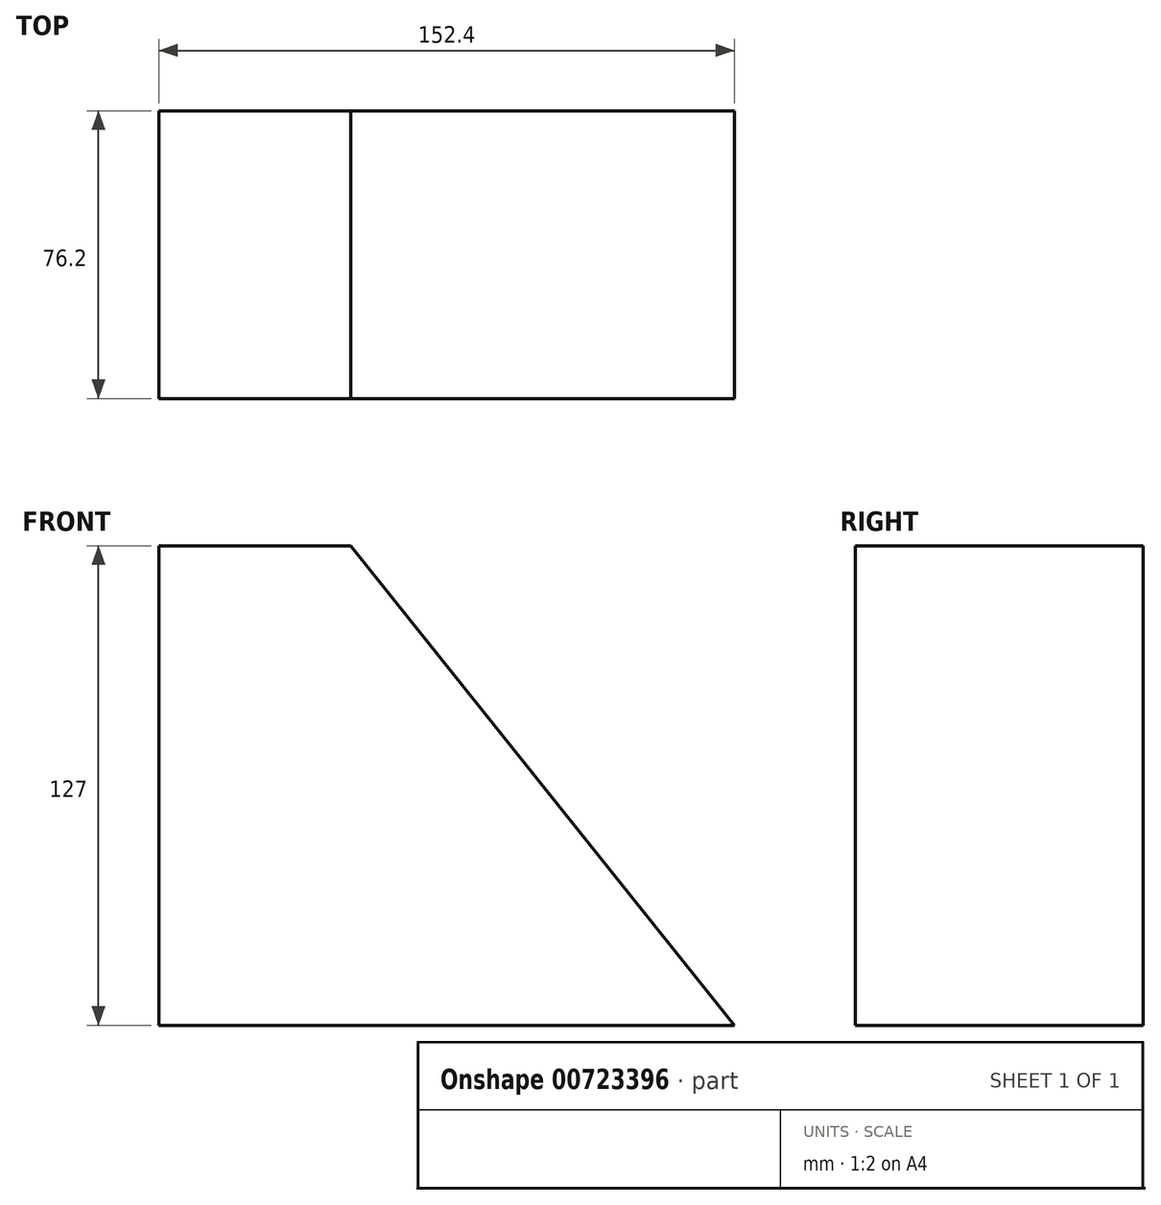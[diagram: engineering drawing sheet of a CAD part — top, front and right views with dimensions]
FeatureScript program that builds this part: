
annotation { "Feature Type Name" : "Feature", "Feature Type Description" : "" }
export const myFeature = defineFeature(function(context is Context, id is Id, definition is map)
    precondition{}
    {
        {
            var Q0;
            Q0=qCreatedBy(makeId("Front.planeOp"),FACE);
            var sketch = newSketch(context, id + "F0", { "sketchPlane" : qUnion([Q0])});
            skLineSegment(sketch, "E0", {"start": v(-85.96, -54.2) * mm, "end": v(66.44, -54.2) * mm});
            skLineSegment(sketch, "E1", {"start": v(-85.96, -54.2) * mm, "end": v(-85.96, 72.8) * mm});
            skLineSegment(sketch, "E2", {"start": v(-85.96, 72.8) * mm, "end": v(-35.16, 72.8) * mm});
            skLineSegment(sketch, "E3", {"start": v(-35.16, 72.8) * mm, "end": v(66.44, -54.2) * mm});
            skSolve(sketch);
        }
        {
            var Q0;
            Q0=makeQuery(id+"F0.imprint","IMPRINT",FACE,{"disambiguationData":[TD([[makeQuery(id+"F0.imprint","IMPRINT",EDGE,{"derivedFrom":sQuery(id+"F0.wireOp",EDGE,"E0")}),1.0]])]});
            extrude(context, id + "F1", {"entities" : qUnion([Q0]), "depth" : 76.2 * mm, "offsetDistance" : 25.4 * mm});
        }
    });
